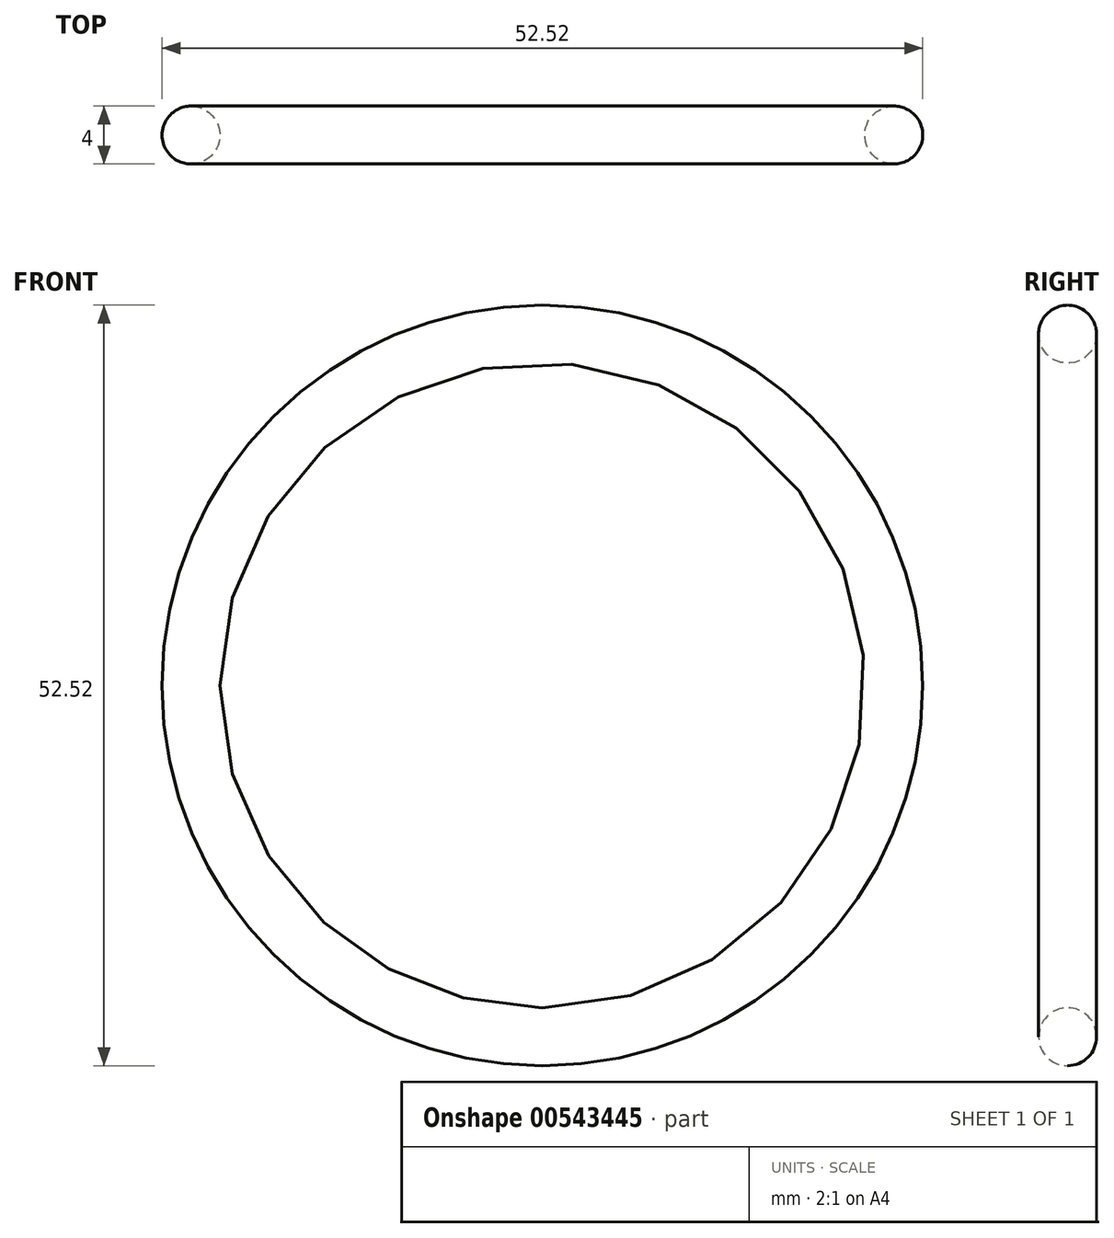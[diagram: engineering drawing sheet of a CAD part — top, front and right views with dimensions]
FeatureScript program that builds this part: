
annotation { "Feature Type Name" : "Feature", "Feature Type Description" : "" }
export const myFeature = defineFeature(function(context is Context, id is Id, definition is map)
    precondition{}
    {
        {
            var Q0;
            Q0=qCreatedBy(makeId("Top.planeOp"),FACE);
            var sketch = newSketch(context, id + "F0", { "sketchPlane" : qUnion([Q0])});
            skCircle(sketch, "E0", {"center": v(-24.26, 0) * mm, "radius": 2 * mm});
            skLineSegment(sketch, "E1", {"start": v(0, 0) * mm, "end": v(0, 13.27) * mm, "construction": true});
            skSolve(sketch);
        }
        {
            var Q0;
            Q0=makeQuery(id+"F0.imprint","IMPRINT",FACE,{"disambiguationData":[TD([[makeQuery(id+"F0.imprint","IMPRINT",EDGE,{"derivedFrom":sQuery(id+"F0.wireOp",EDGE,"E0")}),1.0]])]});
            var Q1;
            Q1=sQuery(id+"F0.wireOp",EDGE,"E1");
            revolve(context, id + "F1", {"entities" : qUnion([Q0]), "axis" : qUnion([Q1]), "revolveType" : RevolveType.FULL});
        }
    });
